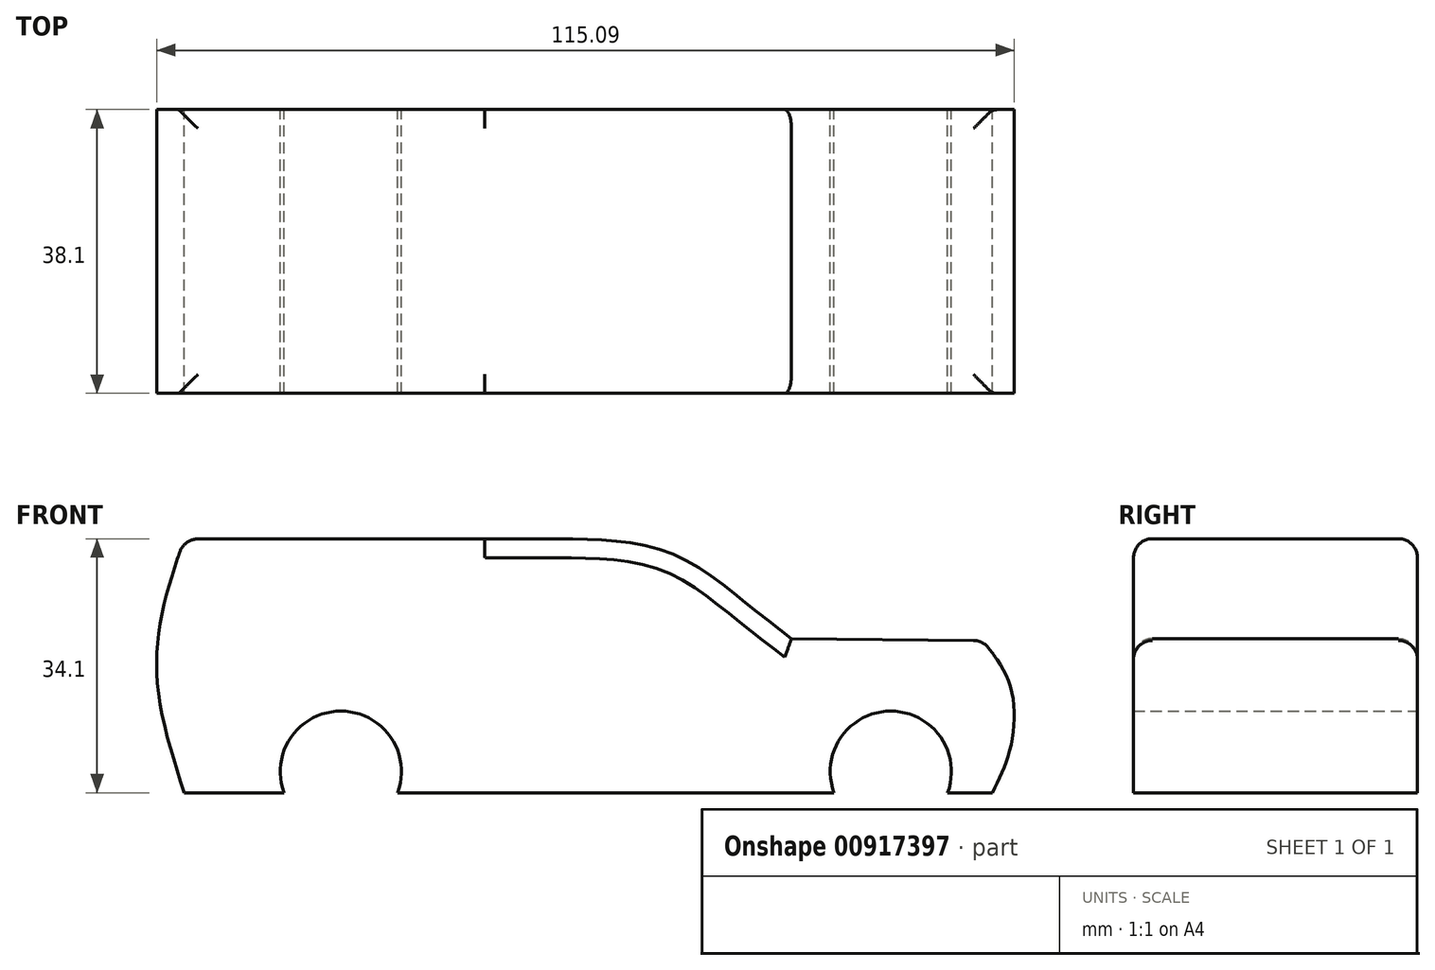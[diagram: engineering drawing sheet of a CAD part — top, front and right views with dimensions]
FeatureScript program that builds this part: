
annotation { "Feature Type Name" : "Feature", "Feature Type Description" : "" }
export const myFeature = defineFeature(function(context is Context, id is Id, definition is map)
    precondition{}
    {
        {
            var Q0;
            Q0=qCreatedBy(makeId("Front.planeOp"),FACE);
            var sketch = newSketch(context, id + "F0", { "sketchPlane" : qUnion([Q0])});
            skFitSpline(sketch, "E0", {"points": [v(63.18, 0) * mm, v(65.59, 6.01) * mm, v(65.59, 14.3) * mm, v(61.85, 20.44) * mm], "startDerivative": vector(8.85, 17.78) * mm, "endDerivative": vector(-13.7, 17.05) * mm});
            skLineSegment(sketch, "E1", {"start": v(61.85, 20.44) * mm, "end": v(36.2, 20.7) * mm});
            skFitSpline(sketch, "E2", {"points": [v(36.2, 20.7) * mm, v(30.05, 25.51) * mm, v(19.9, 32.2) * mm, v(6.81, 34.06) * mm, v(-4.94, 34.06) * mm], "startDerivative": vector(-27.69, 21.29) * mm, "endDerivative": vector(-44.69, -0.4) * mm});
            skLineSegment(sketch, "E3", {"start": v(-4.94, 34.06) * mm, "end": v(-45.28, 34.06) * mm});
            skFitSpline(sketch, "E4", {"points": [v(-45.28, 34.06) * mm, v(-48.22, 24.18) * mm, v(-48.75, 13.5) * mm, v(-45.28, 0) * mm], "startDerivative": vector(-10.68, -31.15) * mm, "endDerivative": vector(12.12, -37.79) * mm});
            skLineSegment(sketch, "E5", {"start": v(-45.28, 0) * mm, "end": v(-31.88, 0) * mm});
            skArc(sketch, "E6", {"start": v(-16.64, 0) * mm, "mid": v(-24.26, 10.96) * mm, "end": v(-31.88, 0) * mm});
            skLineSegment(sketch, "E7", {"start": v(-16.64, 0) * mm, "end": v(41.92, 0) * mm});
            skArc(sketch, "E8", {"start": v(57.16, 0) * mm, "mid": v(49.54, 10.96) * mm, "end": v(41.92, 0) * mm});
            skLineSegment(sketch, "E9", {"start": v(57.16, 0) * mm, "end": v(63.18, 0) * mm});
            skSolve(sketch);
        }
        {
            var Q0;
            Q0 = qSketchRegion(id + "F0", true);
            extrude(context, id + "F1", {"entities" : qUnion([Q0]), "endBound" : BoundingType.SYMMETRIC, "depth" : 38.1 * mm, "offsetDistance" : 25.4 * mm});
        }
        {
            var Q0;
            Q0=makeQuery(id+"F1.opExtrude","CAP_EDGE",EDGE,{"disambiguationData":[OSD([sQuery(id+"F0.wireOp",EDGE,"E1")])],"isStart":false});
            var Q1;
            Q1=makeQuery(id+"F1.opExtrude","CAP_EDGE",EDGE,{"disambiguationData":[OSD([sQuery(id+"F0.wireOp",EDGE,"E1")])],"isStart":true});
            var Q2;
            Q2=makeQuery(id+"F1.opExtrude","SWEPT_EDGE",EDGE,{"disambiguationData":[OSD([sQuery(id+"F0.wireOp",EDGE,"E0"),sQuery(id+"F0.wireOp",EDGE,"E1")])]});
            var Q3;
            Q3=makeQuery(id+"F1.opExtrude","CAP_EDGE",EDGE,{"disambiguationData":[OSD([sQuery(id+"F0.wireOp",EDGE,"E2")])],"isStart":false});
            var Q4;
            Q4=makeQuery(id+"F1.opExtrude","CAP_EDGE",EDGE,{"disambiguationData":[OSD([sQuery(id+"F0.wireOp",EDGE,"E2")])],"isStart":true});
            var Q5;
            Q5=makeQuery(id+"F1.opExtrude","SWEPT_EDGE",EDGE,{"disambiguationData":[OSD([sQuery(id+"F0.wireOp",EDGE,"E3"),sQuery(id+"F0.wireOp",EDGE,"E4")])]});
            fillet(context, id + "F2", {"entities" : qUnion([Q0, Q1, Q2, Q3, Q4, Q5]), "radius" : 2.54 * mm, "tangentPropagation" : true, "allowEdgeOverflow" : false});
        }
        {
            var Q0;
            Q0=makeQuery(id+"F1.opExtrude","CAP_FACE",FACE,{"disambiguationData":[OSD([sQuery(id+"F0.wireOp",EDGE,"E0"),sQuery(id+"F0.wireOp",EDGE,"E1"),sQuery(id+"F0.wireOp",EDGE,"E2"),sQuery(id+"F0.wireOp",EDGE,"E3"),sQuery(id+"F0.wireOp",EDGE,"E4"),sQuery(id+"F0.wireOp",EDGE,"E5"),sQuery(id+"F0.wireOp",EDGE,"E6"),sQuery(id+"F0.wireOp",EDGE,"E7"),sQuery(id+"F0.wireOp",EDGE,"E8"),sQuery(id+"F0.wireOp",EDGE,"E9")])],"isStart":false});
            var sketch = newSketch(context, id + "F3", { "sketchPlane" : qUnion([Q0])});
            skCircle(sketch, "E10", {"center": v(-24.26, 2.83) * mm, "radius": 7.38 * mm});
            skCircle(sketch, "E11", {"center": v(49.54, 2.83) * mm, "radius": 7.38 * mm});
            skSolve(sketch);
        }
        {
            var Q0;
            Q0 = qConstructionFilter(qBodyType(qCreatedBy(id + "F3" ,EDGE), BodyType.WIRE), ConstructionObject.NO);
            extrude(context, id + "F4", {"bodyType" : ToolBodyType.SURFACE, "surfaceEntities" : qUnion([Q0]), "depth" : 1.52 * mm, "offsetDistance" : 25.4 * mm});
        }
        {
            var Q0;
            Q0=makeQuery(id+"F4.opExtrude","SWEPT_BODY",BODY,{"disambiguationData":[OSD([sQuery(id+"F3.wireOp",EDGE,"E10")])]});
            var Q1;
            Q1=makeQuery(id+"F4.opExtrude","SWEPT_BODY",BODY,{"disambiguationData":[OSD([sQuery(id+"F3.wireOp",EDGE,"E11")])]});
            var Q2;
            Q2=qCreatedBy(makeId("Front.planeOp"),FACE);
            mirror(context, id + "F5", {"entities" : qUnion([Q0, Q1]), "mirrorPlane" : qUnion([Q2])});
        }
        {
            var Q0;
            Q0=qCreatedBy(makeId("Right.planeOp"),FACE);
            cPlane(context, id + "F6", {"entities" : qUnion([Q0]), "cplaneType" : CPlaneType.OFFSET, "offset" : 62.23 * mm, "width" : 152.4 * mm, "height" : 152.4 * mm});
        }
    });
